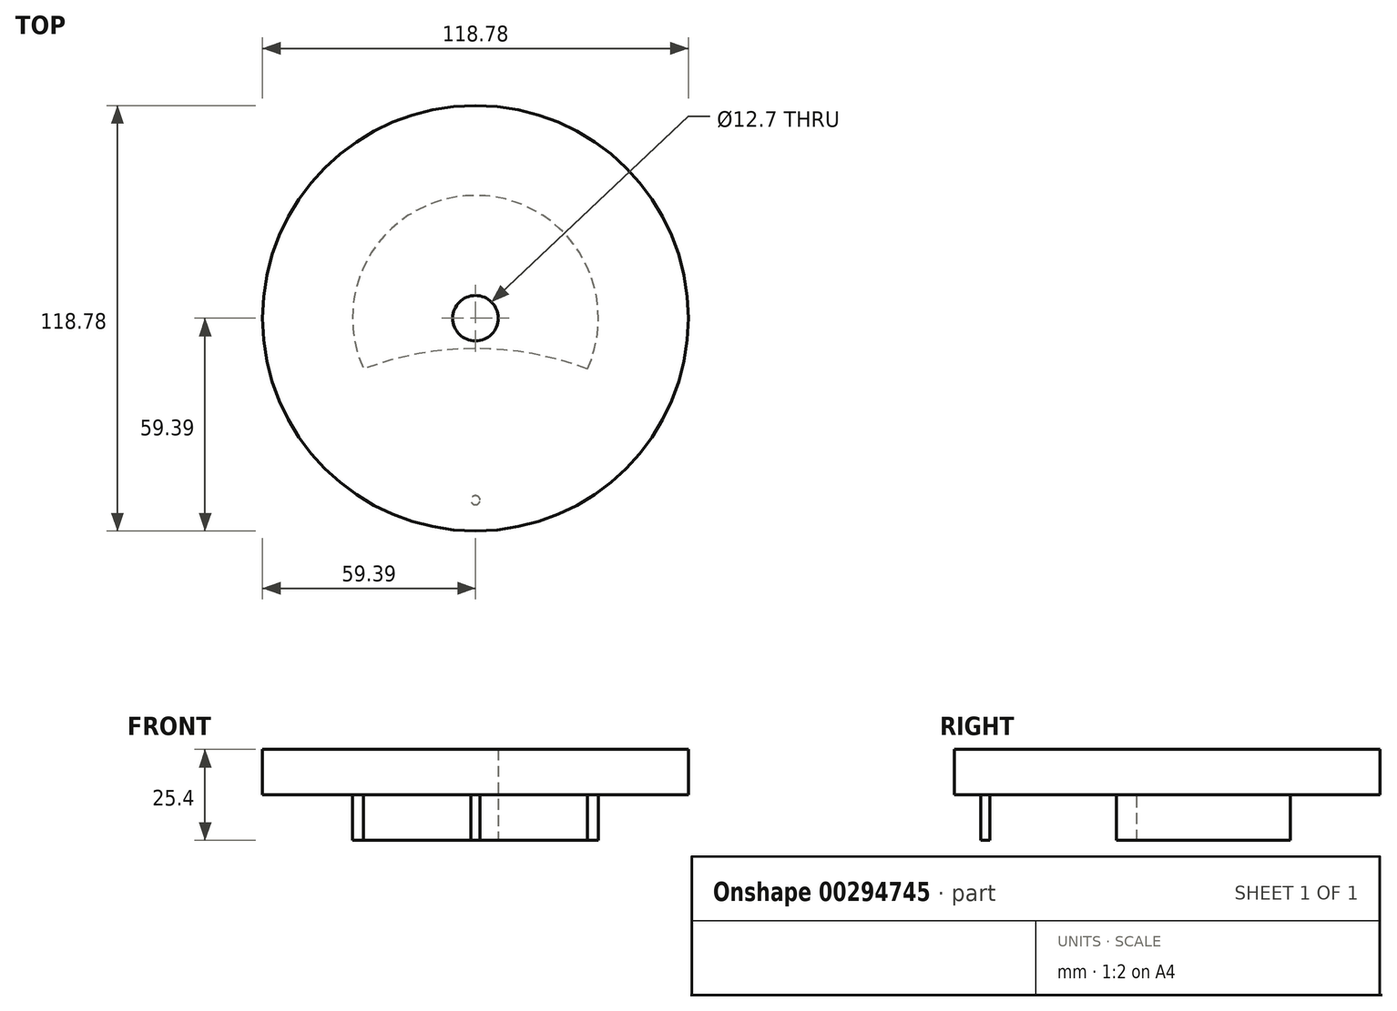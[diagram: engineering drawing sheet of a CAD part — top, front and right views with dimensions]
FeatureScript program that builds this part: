
annotation { "Feature Type Name" : "Feature", "Feature Type Description" : "" }
export const myFeature = defineFeature(function(context is Context, id is Id, definition is map)
    precondition{}
    {
        {
            var Q0;
            Q0=qCreatedBy(makeId("Top.planeOp"),FACE);
            var sketch = newSketch(context, id + "F0", { "sketchPlane" : qUnion([Q0])});
            skLineSegment(sketch, "E0", {"start": v(0, 0) * mm, "end": v(0, 50.8) * mm});
            skLineSegment(sketch, "E1", {"start": v(0, 50.8) * mm, "end": v(87.99, 0) * mm});
            skLineSegment(sketch, "E2", {"start": v(87.99, 0) * mm, "end": v(0, 0) * mm});
            skCircle(sketch, "E3", {"center": v(0, 0) * mm, "radius": 1.27 * mm});
            skCircle(sketch, "E4", {"center": v(0, 50.8) * mm, "radius": 34.3 * mm});
            skCircle(sketch, "E5", {"center": v(0, 50.8) * mm, "radius": 59.4 * mm});
            skCircle(sketch, "E6", {"center": v(0, 50.8) * mm, "radius": 6.35 * mm});
            skCircle(sketch, "E7", {"center": v(0, -45.65) * mm, "radius": 87.99 * mm});
            skSolve(sketch);
        }
        {
            var Q0;
            {var subQ0=sQuery(id+"F0.wireOp",EDGE,"E4");var subQ7=sQuery(id+"F0.wireOp",EDGE,"E0");var subQ8=makeQuery(id+"F0.imprint","INTERSECT",VERTEX,{"derivedFrom":[subQ7,subQ0]});Q0=makeQuery(id+"F0.imprint","IMPRINT",FACE,{"disambiguationData":[TD([[makeQuery(id+"F0.imprint","IMPRINT",EDGE,{"disambiguationData":[TD([[subQ8,-1.0]])],"derivedFrom":subQ7}),1.0]])]});}
            var Q1;
            {var subQ0=sQuery(id+"F0.wireOp",EDGE,"E4");var subQ1=sQuery(id+"F0.wireOp",EDGE,"E0");var subQ2=makeQuery(id+"F0.imprint","INTERSECT",VERTEX,{"derivedFrom":[subQ1,subQ0]});Q1=makeQuery(id+"F0.imprint","IMPRINT",FACE,{"disambiguationData":[TD([[makeQuery(id+"F0.imprint","IMPRINT",EDGE,{"disambiguationData":[TD([[subQ2,-1.0]])],"derivedFrom":subQ1}),-1.0]])]});}
            var Q2;
            {var subQ0=sQuery(id+"F0.wireOp",EDGE,"E3");var subQ1=sQuery(id+"F0.wireOp",EDGE,"E0");var subQ2=makeQuery(id+"F0.imprint","INTERSECT",VERTEX,{"derivedFrom":[subQ1,subQ0]});Q2=makeQuery(id+"F0.imprint","IMPRINT",FACE,{"disambiguationData":[TD([[makeQuery(id+"F0.imprint","IMPRINT",EDGE,{"disambiguationData":[TD([[subQ2,-1.0]])],"derivedFrom":subQ1}),1.0]])]});}
            var Q3;
            {var subQ0=sQuery(id+"F0.wireOp",EDGE,"E7");var subQ1=sQuery(id+"F0.wireOp",EDGE,"E4");var subQ2=makeQuery(id+"F0.imprint","INTERSECT",VERTEX,{"disambiguationData":[OD(0.0)],"derivedFrom":[subQ1,subQ0]});Q3=makeQuery(id+"F0.imprint","IMPRINT",FACE,{"disambiguationData":[TD([[makeQuery(id+"F0.imprint","IMPRINT",EDGE,{"disambiguationData":[TD([[subQ2,1.0]])],"derivedFrom":subQ1}),-1.0]])]});}
            var Q4;
            {var subQ0=sQuery(id+"F0.wireOp",EDGE,"E7");var subQ1=sQuery(id+"F0.wireOp",EDGE,"E4");var subQ2=makeQuery(id+"F0.imprint","INTERSECT",VERTEX,{"disambiguationData":[OD(0.0)],"derivedFrom":[subQ1,subQ0]});Q4=makeQuery(id+"F0.imprint","IMPRINT",FACE,{"disambiguationData":[TD([[makeQuery(id+"F0.imprint","IMPRINT",EDGE,{"disambiguationData":[TD([[subQ2,1.0]])],"derivedFrom":subQ1}),1.0]])]});}
            var Q5;
            {var subQ0=sQuery(id+"F0.wireOp",EDGE,"E5");var subQ1=sQuery(id+"F0.wireOp",EDGE,"E1");var subQ2=makeQuery(id+"F0.imprint","INTERSECT",VERTEX,{"derivedFrom":[subQ1,subQ0]});Q5=makeQuery(id+"F0.imprint","IMPRINT",FACE,{"disambiguationData":[TD([[makeQuery(id+"F0.imprint","IMPRINT",EDGE,{"disambiguationData":[TD([[subQ2,1.0]])],"derivedFrom":subQ1}),1.0]])]});}
            var Q6;
            {var subQ3=sQuery(id+"F0.wireOp",EDGE,"E3");var subQ5=sQuery(id+"F0.wireOp",EDGE,"E0");var subQ6=makeQuery(id+"F0.imprint","INTERSECT",VERTEX,{"derivedFrom":[subQ5,subQ3]});Q6=makeQuery(id+"F0.imprint","IMPRINT",FACE,{"disambiguationData":[TD([[makeQuery(id+"F0.imprint","IMPRINT",EDGE,{"disambiguationData":[TD([[subQ6,-1.0]])],"derivedFrom":subQ5}),-1.0]])]});}
            var Q7;
            {var subQ0=sQuery(id+"F0.wireOp",EDGE,"E7");var subQ1=sQuery(id+"F0.wireOp",EDGE,"E0");var subQ2=makeQuery(id+"F0.imprint","INTERSECT",VERTEX,{"derivedFrom":[subQ1,subQ0]});Q7=makeQuery(id+"F0.imprint","IMPRINT",FACE,{"disambiguationData":[TD([[makeQuery(id+"F0.imprint","IMPRINT",EDGE,{"disambiguationData":[TD([[subQ2,-1.0]])],"derivedFrom":subQ1}),-1.0]])]});}
            var Q8;
            {var subQ0=sQuery(id+"F0.wireOp",EDGE,"E7");var subQ1=sQuery(id+"F0.wireOp",EDGE,"E1");var subQ2=makeQuery(id+"F0.imprint","INTERSECT",VERTEX,{"disambiguationData":[OD(1.0)],"derivedFrom":[subQ1,subQ0]});Q8=makeQuery(id+"F0.imprint","IMPRINT",FACE,{"disambiguationData":[TD([[makeQuery(id+"F0.imprint","IMPRINT",EDGE,{"disambiguationData":[TD([[subQ2,-1.0]])],"derivedFrom":subQ1}),1.0]])]});}
            var Q9;
            {var subQ0=sQuery(id+"F0.wireOp",EDGE,"E2");var subQ1=sQuery(id+"F0.wireOp",EDGE,"E0");var subQ2=makeQuery(id+"F0.imprint","INTERSECT",VERTEX,{"derivedFrom":[subQ1,subQ0]});Q9=makeQuery(id+"F0.imprint","IMPRINT",FACE,{"disambiguationData":[TD([[makeQuery(id+"F0.imprint","IMPRINT",EDGE,{"disambiguationData":[TD([[subQ2,-1.0]])],"derivedFrom":subQ1}),-1.0]])]});}
            var Q10;
            {var subQ0=sQuery(id+"F0.wireOp",EDGE,"E2");var subQ1=sQuery(id+"F0.wireOp",EDGE,"E0");var subQ2=makeQuery(id+"F0.imprint","INTERSECT",VERTEX,{"derivedFrom":[subQ1,subQ0]});Q10=makeQuery(id+"F0.imprint","IMPRINT",FACE,{"disambiguationData":[TD([[makeQuery(id+"F0.imprint","IMPRINT",EDGE,{"disambiguationData":[TD([[subQ2,-1.0]])],"derivedFrom":subQ1}),1.0]])]});}
            extrude(context, id + "F1", {"entities" : qUnion([Q0, Q1, Q2, Q3, Q4, Q5, Q6, Q7, Q8, Q9, Q10]), "depth" : 12.7 * mm});
        }
        {
            var Q0;
            {var subQ0=sQuery(id+"F0.wireOp",EDGE,"E2");var subQ1=sQuery(id+"F0.wireOp",EDGE,"E0");var subQ2=makeQuery(id+"F0.imprint","INTERSECT",VERTEX,{"derivedFrom":[subQ1,subQ0]});Q0=makeQuery(id+"F0.imprint","IMPRINT",FACE,{"disambiguationData":[TD([[makeQuery(id+"F0.imprint","IMPRINT",EDGE,{"disambiguationData":[TD([[subQ2,-1.0]])],"derivedFrom":subQ1}),-1.0]])]});}
            var Q1;
            {var subQ0=sQuery(id+"F0.wireOp",EDGE,"E2");var subQ1=sQuery(id+"F0.wireOp",EDGE,"E0");var subQ2=makeQuery(id+"F0.imprint","INTERSECT",VERTEX,{"derivedFrom":[subQ1,subQ0]});Q1=makeQuery(id+"F0.imprint","IMPRINT",FACE,{"disambiguationData":[TD([[makeQuery(id+"F0.imprint","IMPRINT",EDGE,{"disambiguationData":[TD([[subQ2,-1.0]])],"derivedFrom":subQ1}),1.0]])]});}
            var Q2;
            {var subQ0=sQuery(id+"F0.wireOp",EDGE,"E7");var subQ5=sQuery(id+"F0.wireOp",EDGE,"E0");var subQ10=makeQuery(id+"F0.imprint","INTERSECT",VERTEX,{"derivedFrom":[subQ5,subQ0]});Q2=makeQuery(id+"F0.imprint","IMPRINT",FACE,{"disambiguationData":[TD([[makeQuery(id+"F0.imprint","IMPRINT",EDGE,{"disambiguationData":[TD([[subQ10,-1.0]])],"derivedFrom":subQ5}),1.0]])]});}
            var Q3;
            {var subQ0=sQuery(id+"F0.wireOp",EDGE,"E7");var subQ1=sQuery(id+"F0.wireOp",EDGE,"E0");var subQ2=makeQuery(id+"F0.imprint","INTERSECT",VERTEX,{"derivedFrom":[subQ1,subQ0]});Q3=makeQuery(id+"F0.imprint","IMPRINT",FACE,{"disambiguationData":[TD([[makeQuery(id+"F0.imprint","IMPRINT",EDGE,{"disambiguationData":[TD([[subQ2,-1.0]])],"derivedFrom":subQ1}),-1.0]])]});}
            extrude(context, id + "F2", {"entities" : qUnion([Q0, Q1, Q2, Q3]), "operationType" : NewBodyOperationType.ADD, "oppositeDirection" : true, "depth" : 12.7 * mm});
        }
    });
